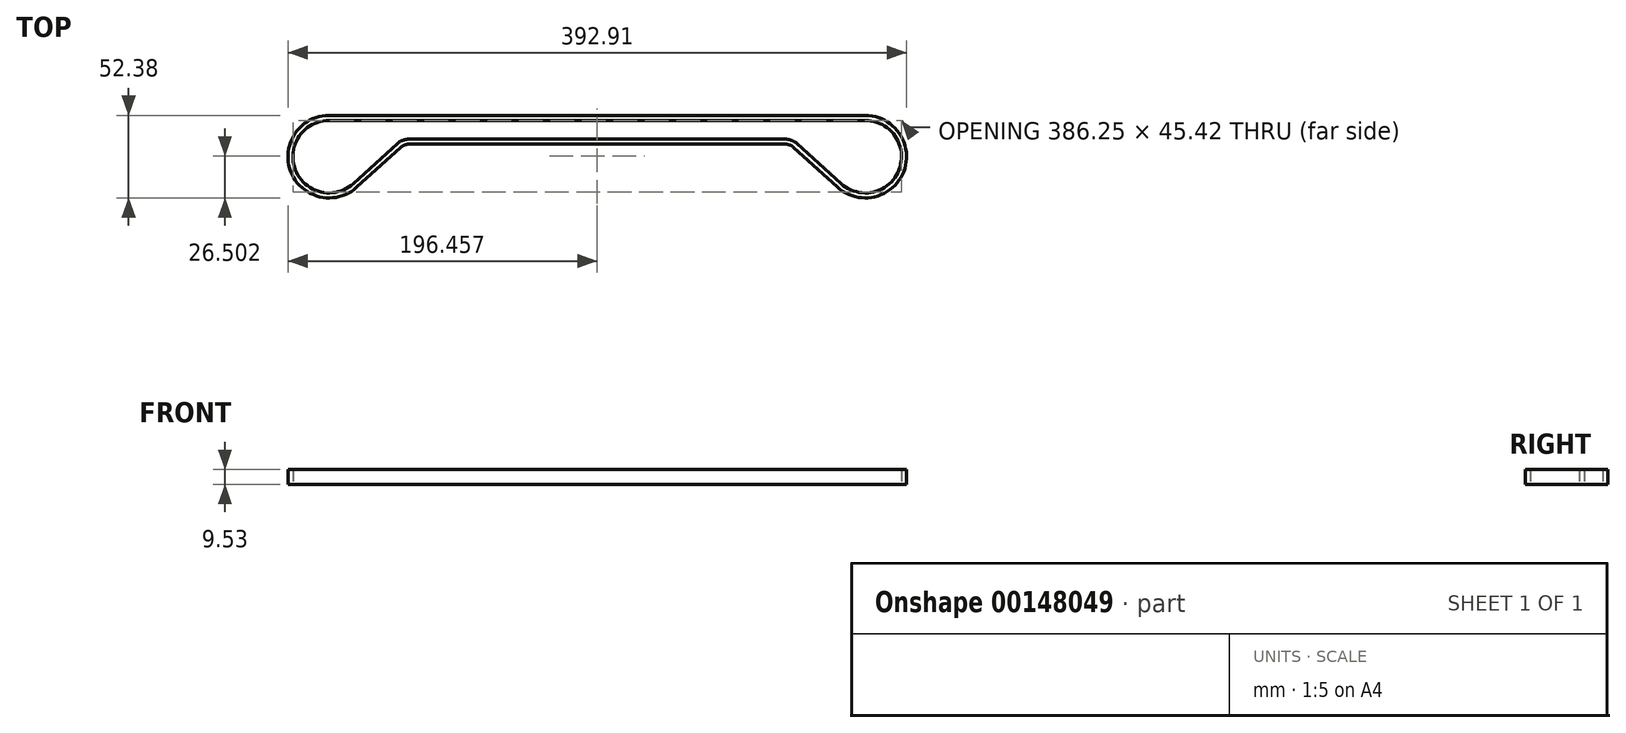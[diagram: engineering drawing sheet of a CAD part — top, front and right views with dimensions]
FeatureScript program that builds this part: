
annotation { "Feature Type Name" : "Feature", "Feature Type Description" : "" }
export const myFeature = defineFeature(function(context is Context, id is Id, definition is map)
    precondition{}
    {
        {
            var Q0;
            Q0=qCreatedBy(makeId("Top.planeOp"),FACE);
            var sketch = newSketch(context, id + "F0", { "sketchPlane" : qUnion([Q0])});
            skArc(sketch, "E0", {"start": v(-15.47, -40.07) * mm, "mid": v(21.47, -31.3) * mm, "end": v(0, 0) * mm});
            skLineSegment(sketch, "E1", {"start": v(0, 0) * mm, "end": v(-340.53, 0) * mm});
            skLineSegment(sketch, "E2", {"start": v(0, 0) * mm, "end": v(0, 3.17) * mm, "construction": true});
            skLineSegment(sketch, "E3", {"start": v(-340.53, 0) * mm, "end": v(-340.53, 3.17) * mm, "construction": true});
            skLineSegment(sketch, "E4", {"start": v(-340.53, 3.17) * mm, "end": v(0, 3.17) * mm});
            skLineSegment(sketch, "E5", {"start": v(-170.26, 0) * mm, "end": v(-170.26, -23.02) * mm, "construction": true});
            skLineSegment(sketch, "E6", {"start": v(-289.73, -23.02) * mm, "end": v(-50.8, -23.02) * mm, "construction": true});
            skArc(sketch, "E7", {"start": v(-45.47, -17.14) * mm, "mid": v(-47.94, -15.61) * mm, "end": v(-50.8, -15.08) * mm});
            skLineSegment(sketch, "E8", {"start": v(-50.8, -15.08) * mm, "end": v(-289.73, -15.08) * mm});
            skLineSegment(sketch, "E9", {"start": v(-50.8, -15.08) * mm, "end": v(-50.8, -11.9) * mm, "construction": true});
            skLineSegment(sketch, "E10", {"start": v(-289.73, -15.08) * mm, "end": v(-289.73, -11.9) * mm, "construction": true});
            skLineSegment(sketch, "E11", {"start": v(-289.73, -11.9) * mm, "end": v(-50.8, -11.9) * mm});
            skArc(sketch, "E12", {"start": v(-43.33, -14.79) * mm, "mid": v(-46.8, -12.65) * mm, "end": v(-50.8, -11.9) * mm});
            skArc(sketch, "E13", {"start": v(-17.6, -42.42) * mm, "mid": v(24.44, -32.45) * mm, "end": v(0, 3.18) * mm});
            skLineSegment(sketch, "E14", {"start": v(-43.33, -14.79) * mm, "end": v(-15.47, -40.07) * mm});
            skLineSegment(sketch, "E15", {"start": v(-45.47, -17.14) * mm, "end": v(-17.6, -42.42) * mm});
            skArc(sketch, "E16", {"start": v(-340.53, 3.17) * mm, "mid": v(-364.96, -32.45) * mm, "end": v(-322.93, -42.42) * mm});
            skArc(sketch, "E17", {"start": v(-340.53, 0) * mm, "mid": v(-362, -31.3) * mm, "end": v(-325.06, -40.07) * mm});
            skArc(sketch, "E18", {"start": v(-289.73, -15.08) * mm, "mid": v(-292.58, -15.61) * mm, "end": v(-295.06, -17.14) * mm});
            skArc(sketch, "E19", {"start": v(-289.73, -11.9) * mm, "mid": v(-293.73, -12.65) * mm, "end": v(-297.2, -14.79) * mm});
            skLineSegment(sketch, "E20", {"start": v(-325.06, -40.07) * mm, "end": v(-297.2, -14.79) * mm});
            skLineSegment(sketch, "E21", {"start": v(-322.93, -42.42) * mm, "end": v(-295.06, -17.14) * mm});
            skLineSegment(sketch, "E22", {"start": v(-50.8, -23.02) * mm, "end": v(0, -23.02) * mm, "construction": true});
            skSolve(sketch);
        }
        {
            var Q0;
            Q0=qSketchRegion(id+"F0",true);
            extrude(context, id + "F1", {"entities" : qUnion([Q0]), "depth" : 9.52 * mm});
        }
    });
